# Revit family: Geryon SRD-S01
name_source: partatom
category: Türen
revit_build: Autodesk Revit 2016 (Build: 20150220_1215(x64)
units: mm (PartAtom-declared; Revit-internal decimal feet)

## family parameters
Beim Laden mit Abzugskörper schneiden = Nein
Gemeinsam genutzt = Nein
Immer vertikal = Ja
OmniClass-Nummer = 23.30.10.00
OmniClass-Titel = Doors
Raumberechnungspunkt = Nein

## types (8) — shared parameters
Analytische Konstruktion = <Keine Auswahl>
CoverMaterial = Glas
CoverWidth = 100 mm  [stored 0.328084 ft]
Design country = Germany
Edition number = 1
ElementWeight = 0.00 kg
FrameMaterial = 1.4401 - A4
Funktion = Außen
GasShellTopFrame 120 = Nein
HasConsoleS1 120 = Nein
HasConsoleS2 120 = Nein
HasLock 120 = Nein
HasLockInside 120 = Nein
HasShellTopFrame 180 = Ja
HasShutOffDevice = Nein
HasShutOffDeviceInside = Nein
HasShutOffDeviceInside120 = Nein
HasShutOffDeviceInside180 = Nein
Hersteller = Kaba GmbH
Konstruktionstyp = Revolving Door
Manufacturer = Kaba GmbH
Manufacturer country = Germany
Manufacturer name = DORMA
Material main = Metal
Material secondary = Glass
Modell = Talos RDR-E01
Nominal height = 2260
OperatingWeight = 0.00 kg
Product SKU = Geryon_SRD-S01
RubberMaterial = Zellkautschuk - EPDM
SectionWidth = 4300 mm
Technical description = http://www.kaba.com
Type = Geryon SRD-S01
URL = http://www.kaba.com
Weight = 0.00 kg
zero-valued in all types: Nominal width

## per-type parameters (varying)
- SRD-S01 v09: AccessLengthOrRadius=980 mm; BaseType=79 mm
79; ClearHeight=2100 mm; ConsoleS1=1031 mm; ConsoleS2=1031 mm; ConsoleType=console : Type 5; Diameter=1010 mm; DiameterCoverFront=1090 mm; DiameterGlassInside=989 mm; DiameterGlassOutside=1001 mm; DiameterNightLock=1040 mm; DiameterNightLockCover=1070 mm; DiameterNightLockFrame=1031 mm; DiameterNightLockGlassInside=1049 mm; DiameterNightLockGlassOutside=1060 mm; Dicke=25 mm  [stored 0.082021 ft]; DoorThickness=25 mm  [stored 0.082021 ft]; DoorWidth=940 mm  [stored 3.08399 ft]; FrameHeight=2200 mm; FrameThickness=49 mm  [stored 0.160761 ft]; FrameThicknessCenter=61 mm; GlassRoofDownside=2179 mm; GlassRoofTopside=2192 mm; GlassRoofWithFrame=Ja; HandleMaterial=PA6.6 Gf30(schwarz); HasCentralColumn=Nein; HasCentralColumn 120=Nein; HasCentralColumn 180=Nein; HasConsoleS1=Nein; HasConsoleS1 180=Nein; HasConsoleS2=Nein; HasConsoleS2 180=Nein; HasGrabHandles=Ja; HasGrabHandles 120=Nein; HasGrabHandles 180=Ja; HasHandleBar=Nein; HasLock=Nein; HasLock 180=Nein; HasLockInside=Nein; HasLockInside 180=Nein; HasRoofGlassOnly=Nein; Height=2200 mm; MotorDriveType=-; OuterDiameter=2100 mm; ProfileCenter=7.5 mm; ProfileWidth=40 mm  [stored 0.131234 ft]; RotationInterval 120=Nein; RotationInterval 180=Ja; StandardUsed=9; Width=2000 mm
- SRD-S01 v10: AccessLengthOrRadius=880 mm; BaseType=69 mm / 370 mm
79; ClearHeight=2200 mm; ConsoleS1=931 mm  [stored 3.05446 ft]; ConsoleS2=931 mm  [stored 3.05446 ft]; ConsoleType=console : Type 5; Diameter=910 mm  [stored 2.98556 ft]; DiameterCoverFront=990 mm  [stored 3.24803 ft]; DiameterGlassInside=889 mm; DiameterGlassOutside=901 mm; DiameterNightLock=940 mm  [stored 3.08399 ft]; DiameterNightLockCover=970 mm; DiameterNightLockFrame=931 mm  [stored 3.05446 ft]; DiameterNightLockGlassInside=949 mm  [stored 3.11352 ft]; DiameterNightLockGlassOutside=960 mm; Dicke=40 mm  [stored 0.131234 ft]; DoorThickness=40 mm  [stored 0.131234 ft]; DoorWidth=840 mm  [stored 2.75591 ft]; FrameHeight=2300 mm; FrameThickness=63 mm  [stored 0.206693 ft]; FrameThicknessCenter=75 mm; GlassRoofDownside=2279 mm; GlassRoofTopside=2292 mm; GlassRoofWithFrame=Ja; HandleMaterial=1.4401 - A4; HasCentralColumn=Ja; HasCentralColumn 120=Ja; HasCentralColumn 180=Nein; HasConsoleS1=Nein; HasConsoleS1 180=Nein; HasConsoleS2=Nein; HasConsoleS2 180=Nein; HasGrabHandles=Nein; HasGrabHandles 120=Ja; HasGrabHandles 180=Nein; HasHandleBar=Ja; HasLock=Nein; HasLock 180=Nein; HasLockInside=Nein; HasLockInside 180=Nein; HasRoofGlassOnly=Nein; Height=2300 mm; MotorDriveType=K8-SA1; OuterDiameter=1900 mm; ProfileCenter=0 mm  [stored 0 ft]; ProfileWidth=40 mm  [stored 0.131234 ft]; RotationInterval 120=Ja; RotationInterval 180=Nein; StandardUsed=10; Width=1800 mm
- SRD-S01 v11: AccessLengthOrRadius=830 mm; BaseType=69 mm / 405 mm
79; ClearHeight=2300 mm; ConsoleS1=881 mm  [stored 2.89042 ft]; ConsoleS2=881 mm  [stored 2.89042 ft]; ConsoleType=console : Type 5; Diameter=860 mm; DiameterCoverFront=940 mm  [stored 3.08399 ft]; DiameterGlassInside=839 mm; DiameterGlassOutside=851 mm; DiameterNightLock=890 mm  [stored 2.91995 ft]; DiameterNightLockCover=920 mm; DiameterNightLockFrame=881 mm  [stored 2.89042 ft]; DiameterNightLockGlassInside=899 mm  [stored 2.94948 ft]; DiameterNightLockGlassOutside=910 mm  [stored 2.98556 ft]; Dicke=25 mm  [stored 0.082021 ft]; DoorThickness=25 mm  [stored 0.082021 ft]; DoorWidth=790 mm  [stored 2.59186 ft]; FrameHeight=2400 mm; FrameThickness=49 mm  [stored 0.160761 ft]; FrameThicknessCenter=61 mm; GlassRoofDownside=2379 mm; GlassRoofTopside=2392 mm; GlassRoofWithFrame=Ja; HandleMaterial=1.4401 - A4; HasCentralColumn=Nein; HasCentralColumn 120=Nein; HasCentralColumn 180=Nein; HasConsoleS1=Nein; HasConsoleS1 180=Nein; HasConsoleS2=Nein; HasConsoleS2 180=Nein; HasGrabHandles=Nein; HasGrabHandles 120=Nein; HasGrabHandles 180=Ja; HasHandleBar=Ja; HasLock=Nein; HasLock 180=Nein; HasLockInside=Nein; HasLockInside 180=Nein; HasRoofGlassOnly=Nein; Height=2400 mm; MotorDriveType=K8-SA2; OuterDiameter=1800 mm; ProfileCenter=7.5 mm; ProfileWidth=40 mm  [stored 0.131234 ft]; RotationInterval 120=Nein; RotationInterval 180=Ja; StandardUsed=11; Width=1700 mm
- SRD-S01 v12: AccessLengthOrRadius=880 mm; BaseType=69 mm / 440 mm
79; ClearHeight=2400 mm; ConsoleS1=931 mm  [stored 3.05446 ft]; ConsoleS2=931 mm  [stored 3.05446 ft]; ConsoleType=console : Type 5; Diameter=910 mm  [stored 2.98556 ft]; DiameterCoverFront=990 mm  [stored 3.24803 ft]; DiameterGlassInside=889 mm; DiameterGlassOutside=901 mm; DiameterNightLock=940 mm  [stored 3.08399 ft]; DiameterNightLockCover=970 mm; DiameterNightLockFrame=931 mm  [stored 3.05446 ft]; DiameterNightLockGlassInside=949 mm  [stored 3.11352 ft]; DiameterNightLockGlassOutside=960 mm; Dicke=25 mm  [stored 0.082021 ft]; DoorThickness=25 mm  [stored 0.082021 ft]; DoorWidth=840 mm  [stored 2.75591 ft]; FrameHeight=2413 mm; FrameThickness=49 mm  [stored 0.160761 ft]; FrameThicknessCenter=61 mm; GlassRoofDownside=2479 mm; GlassRoofTopside=2492 mm; GlassRoofWithFrame=Nein; HandleMaterial=PA6.6 Gf30(schwarz); HasCentralColumn=Nein; HasCentralColumn 120=Nein; HasCentralColumn 180=Nein; HasConsoleS1=Nein; HasConsoleS1 180=Nein; HasConsoleS2=Nein; HasConsoleS2 180=Nein; HasGrabHandles=Ja; HasGrabHandles 120=Nein; HasGrabHandles 180=Ja; HasHandleBar=Nein; HasLock=Nein; HasLock 180=Nein; HasLockInside=Nein; HasLockInside 180=Nein; HasRoofGlassOnly=Ja; Height=2500 mm; MotorDriveType=-; OuterDiameter=1900 mm; ProfileCenter=7.5 mm; ProfileWidth=40 mm  [stored 0.131234 ft]; RotationInterval 120=Nein; RotationInterval 180=Ja; StandardUsed=12; Width=1800 mm
- SRD-S01 v13: AccessLengthOrRadius=980 mm; BaseType=300 mm / 475 mm
79; ClearHeight=2400 mm; ConsoleS1=1031 mm; ConsoleS2=1031 mm; ConsoleType=console : Type 5; Diameter=1010 mm; DiameterCoverFront=1090 mm; DiameterGlassInside=989 mm; DiameterGlassOutside=1001 mm; DiameterNightLock=1040 mm; DiameterNightLockCover=1070 mm; DiameterNightLockFrame=1031 mm; DiameterNightLockGlassInside=1049 mm; DiameterNightLockGlassOutside=1060 mm; Dicke=25 mm  [stored 0.082021 ft]; DoorThickness=25 mm  [stored 0.082021 ft]; DoorWidth=940 mm  [stored 3.08399 ft]; FrameHeight=2413 mm; FrameThickness=49 mm  [stored 0.160761 ft]; FrameThicknessCenter=61 mm; GlassRoofDownside=2479 mm; GlassRoofTopside=2492 mm; GlassRoofWithFrame=Nein; HandleMaterial=PA6.6 Gf30(schwarz); HasCentralColumn=Nein; HasCentralColumn 120=Nein; HasCentralColumn 180=Nein; HasConsoleS1=Nein; HasConsoleS1 180=Nein; HasConsoleS2=Nein; HasConsoleS2 180=Nein; HasGrabHandles=Ja; HasGrabHandles 120=Nein; HasGrabHandles 180=Ja; HasHandleBar=Nein; HasLock=Nein; HasLock 180=Nein; HasLockInside=Nein; HasLockInside 180=Nein; HasRoofGlassOnly=Ja; Height=2500 mm; MotorDriveType=-; OuterDiameter=2100 mm; ProfileCenter=7.5 mm; ProfileWidth=40 mm  [stored 0.131234 ft]; RotationInterval 120=Nein; RotationInterval 180=Ja; StandardUsed=13; Width=2000 mm
- SRD-S01 v14: AccessLengthOrRadius=930 mm; BaseType=330 mm / 510 mm
79; ClearHeight=2200 mm; ConsoleS1=1029 mm; ConsoleS2=1029 mm; ConsoleType=console : Type 4; Diameter=960 mm; DiameterCoverFront=1040 mm; DiameterGlassInside=939 mm; DiameterGlassOutside=951 mm; DiameterNightLock=990 mm  [stored 3.24803 ft]; DiameterNightLockCover=1020 mm; DiameterNightLockFrame=981 mm  [stored 3.2185 ft]; DiameterNightLockGlassInside=999 mm; DiameterNightLockGlassOutside=1010 mm; Dicke=25 mm  [stored 0.082021 ft]; DoorThickness=25 mm  [stored 0.082021 ft]; DoorWidth=890 mm  [stored 2.91995 ft]; FrameHeight=2300 mm; FrameThickness=49 mm  [stored 0.160761 ft]; FrameThicknessCenter=61 mm; GlassRoofDownside=2279 mm; GlassRoofTopside=2292 mm; GlassRoofWithFrame=Ja; HandleMaterial=PA6.6 Gf30(schwarz); HasCentralColumn=Nein; HasCentralColumn 120=Nein; HasCentralColumn 180=Nein; HasConsoleS1=Ja; HasConsoleS1 180=Ja; HasConsoleS2=Ja; HasConsoleS2 180=Ja; HasGrabHandles=Ja; HasGrabHandles 120=Nein; HasGrabHandles 180=Ja; HasHandleBar=Nein; HasLock=Ja; HasLock 180=Ja; HasLockInside=Ja; HasLockInside 180=Ja; HasRoofGlassOnly=Nein; Height=2300 mm; MotorDriveType=K8-SA1; OuterDiameter=2000 mm; ProfileCenter=7.5 mm; ProfileWidth=40 mm  [stored 0.131234 ft]; RotationInterval 120=Nein; RotationInterval 180=Ja; StandardUsed=14; Width=1900 mm
- SRD-S01 v15: AccessLengthOrRadius=880 mm; BaseType=360 mm / 545 mm
79; ClearHeight=2300 mm; ConsoleS1=979 mm; ConsoleS2=979 mm; ConsoleType=console : Type 5; Diameter=910 mm  [stored 2.98556 ft]; DiameterCoverFront=990 mm  [stored 3.24803 ft]; DiameterGlassInside=889 mm; DiameterGlassOutside=901 mm; DiameterNightLock=940 mm  [stored 3.08399 ft]; DiameterNightLockCover=970 mm; DiameterNightLockFrame=931 mm  [stored 3.05446 ft]; DiameterNightLockGlassInside=949 mm  [stored 3.11352 ft]; DiameterNightLockGlassOutside=960 mm; Dicke=56 mm; DoorThickness=56 mm; DoorWidth=840 mm  [stored 2.75591 ft]; FrameHeight=2400 mm; FrameThickness=80 mm; FrameThicknessCenter=92 mm; GlassRoofDownside=2379 mm; GlassRoofTopside=2392 mm; GlassRoofWithFrame=Ja; HandleMaterial=PA6.6 Gf30(schwarz); HasCentralColumn=Ja; HasCentralColumn 120=Nein; HasCentralColumn 180=Ja; HasConsoleS1=Ja; HasConsoleS1 180=Ja; HasConsoleS2=Ja; HasConsoleS2 180=Ja; HasGrabHandles=Ja; HasGrabHandles 120=Nein; HasGrabHandles 180=Ja; HasHandleBar=Nein; HasLock=Ja; HasLock 180=Ja; HasLockInside=Ja; HasLockInside 180=Ja; HasRoofGlassOnly=Nein; Height=2400 mm; MotorDriveType=K8-SA2; OuterDiameter=1900 mm; ProfileCenter=0 mm  [stored 0 ft]; ProfileWidth=56 mm; RotationInterval 120=Nein; RotationInterval 180=Ja; StandardUsed=15; Width=1800 mm
- SRD-S01 v16: AccessLengthOrRadius=830 mm; BaseType=390 mm / 580 mm
79; ClearHeight=2400 mm; ConsoleS1=929 mm  [stored 3.0479 ft]; ConsoleS2=929 mm  [stored 3.0479 ft]; ConsoleType=console : Type 5; Diameter=860 mm; DiameterCoverFront=940 mm  [stored 3.08399 ft]; DiameterGlassInside=839 mm; DiameterGlassOutside=851 mm; DiameterNightLock=890 mm  [stored 2.91995 ft]; DiameterNightLockCover=920 mm; DiameterNightLockFrame=881 mm  [stored 2.89042 ft]; DiameterNightLockGlassInside=899 mm  [stored 2.94948 ft]; DiameterNightLockGlassOutside=910 mm  [stored 2.98556 ft]; Dicke=40 mm  [stored 0.131234 ft]; DoorThickness=40 mm  [stored 0.131234 ft]; DoorWidth=790 mm  [stored 2.59186 ft]; FrameHeight=2500 mm; FrameThickness=63 mm  [stored 0.206693 ft]; FrameThicknessCenter=75 mm; GlassRoofDownside=2479 mm; GlassRoofTopside=2492 mm; GlassRoofWithFrame=Ja; HandleMaterial=1.4401 - A4; HasCentralColumn=Ja; HasCentralColumn 120=Nein; HasCentralColumn 180=Ja; HasConsoleS1=Nein; HasConsoleS1 180=Nein; HasConsoleS2=Nein; HasConsoleS2 180=Nein; HasGrabHandles=Nein; HasGrabHandles 120=Nein; HasGrabHandles 180=Ja; HasHandleBar=Ja; HasLock=Ja; HasLock 180=Ja; HasLockInside=Ja; HasLockInside 180=Ja; HasRoofGlassOnly=Nein; Height=2500 mm; MotorDriveType=K8-SA1; OuterDiameter=1800 mm; ProfileCenter=0 mm  [stored 0 ft]; ProfileWidth=40 mm  [stored 0.131234 ft]; RotationInterval 120=Nein; RotationInterval 180=Ja; StandardUsed=16; Width=1700 mm

note: [stored X ft] marks values corroborated as IEEE doubles in the binary element streams (Revit-internal decimal feet)
